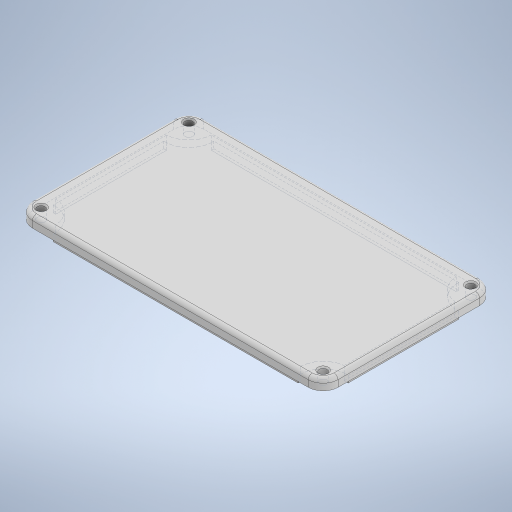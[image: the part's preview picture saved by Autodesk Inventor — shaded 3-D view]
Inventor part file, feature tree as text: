
AUTODESK INVENTOR PART (.ipt)
format: ipt  version: 2023 (Build 270158030, 158C)  size: 603,648 bytes
history: native  units: mm
features: sketch x8, extrude x6, other x4, fillet x3, hole x2, plane x1
ambient origin geometry x8: Origin, YZ Plane, XZ Plane, XY Plane, X Axis, Y Axis, Z Axis, Center Point
bodies: Body1 (feature_tree), Body2 (feature_tree)
feature tree (24):
  other  "Die Cast Box"
  other  "Annotations"
  extrude  "Extrusion1"  Depth=63.6mm
  sketch  "Sketch2"  dims[d2=5.0mm d10=26.3mm d11=0.261799mm]
  plane  "Work Plane1"
  extrude  "Extrusion2"  Depth=5.0mm
  extrude  "Extrusion3"  Depth=1.5mm
  fillet  "Fillet1"  Radius=1.5mm
  sketch  "Sketch4"  dims[d16=4.0mm d17=-1.5mm d18=26.3mm d19=-0.261799mm]
  fillet  "Fillet2"  Radius=1.5mm
  hole  "Hole1"  [1 undecoded]
  extrude  "Extrusion4"  Depth=4.0mm
  fillet  "Fillet3"  Radius=5.3mm
  hole  "Hole2"  [1 undecoded]
  extrude  "Extrusion5"  Depth=3.8mm
  extrude  "Extrusion6"  Depth=1.5mm
  sketch  "Sketch1"  dims[d0=114.5mm d1=63.6mm]
  sketch  "Sketch3"  dims[d12=1.5mm d13=1.5mm d14=1.5mm d15=1.5mm]
  sketch  "Sketch5"  dims[d20=4.0mm d21=4.0mm d22=5.3mm]
  other  "Die Cast Lid"
  sketch  "Sketch6"  dims[d23=3.8mm d24=3.8mm]
  sketch  "Sketch7"  dims[d25=3.8mm d26=3.8mm]
  sketch  "Sketch8"  dims[d27=10.0mm d28=0.0mm d29=1.5mm d30=3.0mm d31=2.0mm d32=2.85mm d33=7.0mm d34=4.0mm d35=2.0mm d36=90.0deg d37=20.0mm d38=20.594885mm d39=5.67mm d40=4.0mm d41=0.0mm d42=1.5mm d43=3.0mm d44=3.0mm d45=7.0mm d46=4.0mm d47=2.0mm d48=90.0deg d49=4.0mm d50=20.594885mm d51=0.5mm d52=0.5mm d53=0.5mm d54=0.5mm d55=1.5mm d56=1.5mm d57=1.5mm d58=1.5mm d59=0.5mm d60=0.5mm d62=10.0mm d63=10.0mm d64=10.0mm d65=10.0mm d66=2.5mm d67=0.0mm d71=9.0mm d72=9.0mm d73=9.0mm d74=9.0mm d75=1.0mm d76=2.5mm d77=0.0mm]
  other  "General Note 1"
note: 2 required parameter values undecoded (feature->parameter linkage not recoverable at this tier; creation-order binding heuristic only, values carry confidence <= 0.55)
